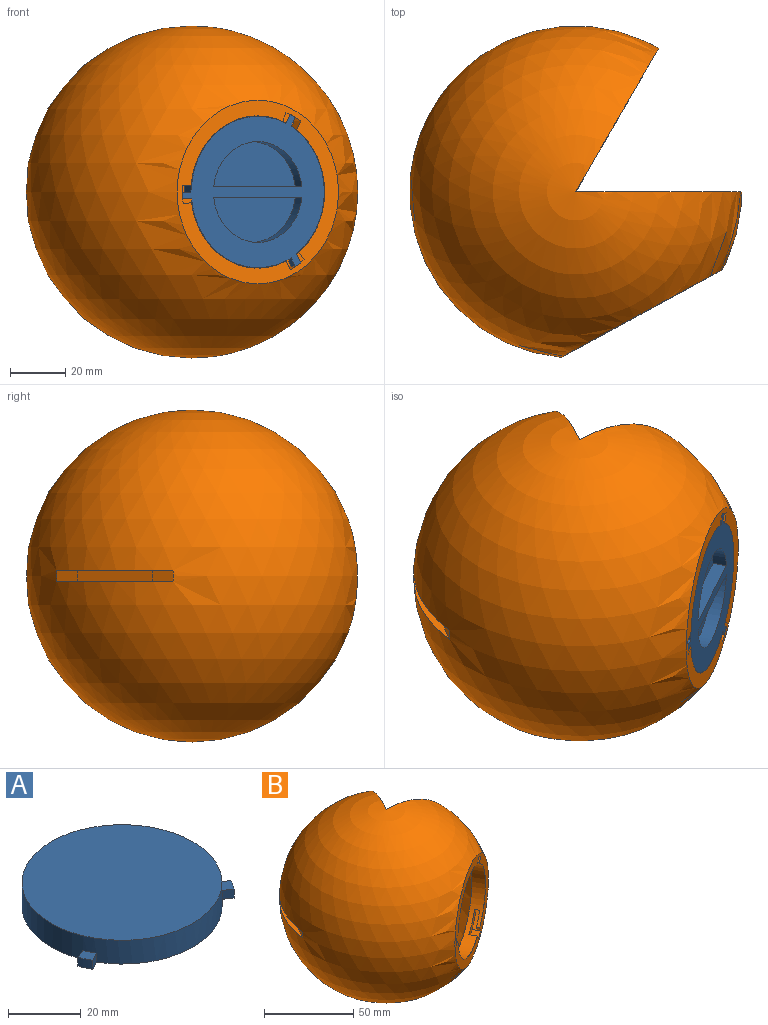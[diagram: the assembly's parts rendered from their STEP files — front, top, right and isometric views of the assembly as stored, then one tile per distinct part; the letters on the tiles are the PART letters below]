
ASSEMBLY  parts=2 mates=1
PART A: 21 faces, bbox 56.2x58.5x8 mm
  f0: plane 58.5x56.24mm, normal (0,0,-1), area 1519.9mm2, adj f1,f3,f4,f5,f7,f8,f9,f11
  f1: cylinder r=27.5mm len=55mm, axis (0,0,-1), area 1347.7mm2, adj f0,f2,f3,f4,f6,f7,f8,f10
  f2: plane 55x55mm, normal (0,0,1), area 2375.8mm2, adj f1
  f3: plane 3.5x3mm, normal (-1,0,0), area 10.5mm2, adj f0,f1,f5,f6
  f4: plane 3.47x3mm, normal (0.99,-0.14,0), area 10.5mm2, adj f0,f1,f5,f6
  f5: cylinder r=31mm len=4.31mm, axis (0,0,-1), area 13mm2, adj f0,f3,f4,f6
  f6: plane 4.31x3.77mm, normal (0,0,1), area 14.3mm2, adj f1,f3,f4,f5
  f7: plane 3.25x3mm, normal (-0.37,0.93,0), area 10.5mm2, adj f0,f1,f9,f10
  f8: plane 3.03x3mm, normal (0.5,-0.87,0), area 10.5mm2, adj f0,f1,f9,f10
  f9: cylinder r=31mm len=3.89mm, axis (0,0,-1), area 13mm2, adj f0,f7,f8,f10
  f10: plane 5.2x4.93mm, normal (0,0,1), area 14.3mm2, adj f1,f7,f8,f9
  f11: plane 3x2.76mm, normal (-0.62,-0.79,0), area 10.5mm2, adj f0,f1,f13,f14
  f12: plane 3.03x3mm, normal (0.5,0.87,0), area 10.5mm2, adj f0,f1,f13,f14
  f13: cylinder r=31mm len=3.59mm, axis (0,0,-1), area 13mm2, adj f0,f11,f12,f14
  f14: plane 5.34x5.18mm, normal (0,0,1), area 14.3mm2, adj f1,f11,f12,f13
  f15: plane 36.25x5mm, normal (1,0,0), area 181.2mm2, adj f0,f16,f17
  f16: cylinder r=18.23mm len=36.25mm, axis (0,0,-1), area 266.4mm2, adj f0,f15,f17
  f17: plane 36.25x16.23mm, normal (0,0,-1), area 449.4mm2, adj f15,f16
  f18: plane 36.25x5mm, normal (-1,0,0), area 181.2mm2, adj f0,f19,f20
  f19: cylinder r=18.23mm len=36.25mm, axis (0,0,-1), area 266.4mm2, adj f0,f18,f20
  f20: plane 36.25x16.23mm, normal (0,0,-1), area 449.4mm2, adj f18,f19
PART B: 38 faces, bbox 120x120x120 mm
  f0: plane 5.75x4.44mm, normal (0,0,1), area 7.7mm2, adj f5,f6,f7,f26,f27,f36,f37
  f1: plane 5.31x3.31mm, normal (0.76,0.41,-0.5), area 7.7mm2, adj f3,f6,f7,f23,f25,f33,f34
  f2: plane 5.31x3.31mm, normal (-0.76,-0.41,-0.5), area 7.7mm2, adj f4,f6,f7,f20,f22,f30,f31
  f3: sphere r=57mm, area 7.9mm2, adj f1,f6,f7,f28
  f4: sphere r=57mm, area 7.9mm2, adj f2,f6,f7,f24
  f5: sphere r=57mm, area 7.9mm2, adj f0,f6,f7,f21
  f6: plane 66.33x58.27mm, normal (0.48,-0.88,0), area 1046.5mm2, adj f0,f1,f2,f3,f4,f5,f8,f21
  f7: cylinder r=27.5mm len=55mm, axis (0.48,-0.88,0), area 1204.7mm2, adj f0,f1,f2,f3,f4,f5,f19,f20
  f8: sphere r=60mm, area 33727mm2, adj f6,f10,f11,f14,f15,f16,f17
  f9: sphere r=57mm, area 29129.7mm2, adj f12,f13,f14,f15,f16,f17,f18
  f10: plane 120x51.96mm, normal (0.87,-0.5,0), area 5654.9mm2, adj f8,f11
  f11: plane 120x60mm, normal (0,1,0), area 5654.9mm2, adj f8,f10
  f12: plane 113.84x53.8mm, normal (-0.87,0.5,0), area 5680.1mm2, adj f9,f13
  f13: plane 113.84x62.12mm, normal (0,-1,0), area 5680.1mm2, adj f9,f12
  f14: plane 7.61x4.5mm, normal (-0.86,0.51,0), area 34.9mm2, adj f8,f9,f16,f17
  f15: plane 7.61x4.5mm, normal (-0.86,0.51,0), area 34.9mm2, adj f8,f9,f16,f17
  f16: plane 42.02x24.85mm, normal (0,0,1), area 124.6mm2, adj f8,f9,f14,f15
  f17: plane 42.02x24.85mm, normal (0,0,-1), area 124.6mm2, adj f8,f9,f14,f15
  f18: cylinder r=32.5mm len=65mm, axis (0.48,-0.88,0), area 985.7mm2, adj f9,f19
  f19: plane 65x57.09mm, normal (-0.48,0.88,0), area 942.5mm2, adj f7,f18
  f20: plane 12.91x12.58mm, normal (0.48,-0.88,0), area 57.2mm2, adj f2,f7,f21,f22,f29,f30
  f21: plane 5.31x4.01mm, normal (0.76,0.41,0.5), area 18.5mm2, adj f5,f6,f7,f20,f22
  f22: plane 6.46x6.19mm, normal (-0.44,-0.24,0.87), area 25mm2, adj f2,f6,f20,f21
  f23: plane 13.99x8.55mm, normal (0.48,-0.88,0), area 57.2mm2, adj f1,f7,f24,f25,f32,f33
  f24: plane 5.31x4.01mm, normal (-0.76,-0.41,0.5), area 18.5mm2, adj f4,f6,f7,f23,f25
  f25: plane 6.46x6.19mm, normal (-0.44,-0.24,-0.87), area 25mm2, adj f1,f6,f23,f24
  f26: plane 16.27x5.64mm, normal (0.48,-0.88,0), area 57.2mm2, adj f0,f7,f27,f28,f35,f36
  f27: plane 5x4.39mm, normal (0.88,0.48,0), area 25mm2, adj f0,f6,f26,f28
  f28: plane 6.16x5.75mm, normal (0,0,-1), area 18.5mm2, adj f3,f6,f7,f26,f27
  f29: plane 4.06x4.05mm, normal (-0.49,-0.27,-0.83), area 10.7mm2, adj f7,f20,f30,f31
  f30: cylinder r=31.08mm len=8.64mm, axis (-0.48,0.88,0), area 35.3mm2, adj f2,f20,f29,f31
  f31: plane 10.32x8.78mm, normal (-0.48,0.88,0), area 39.1mm2, adj f2,f7,f29,f30
  f32: plane 3.57x2.75mm, normal (0.88,0.48,-0.06), area 10.7mm2, adj f7,f23,f33,f34
  f33: cylinder r=31.08mm len=11.38mm, axis (-0.48,0.88,0), area 35.3mm2, adj f1,f23,f32,f34
  f34: plane 10.14x6.05mm, normal (-0.48,0.88,0), area 39.1mm2, adj f1,f7,f32,f33
  f35: plane 4.25x4.17mm, normal (-0.39,-0.21,0.9), area 10.7mm2, adj f7,f26,f36,f37
  f36: cylinder r=31.08mm len=11.27mm, axis (-0.48,0.88,0), area 35.3mm2, adj f0,f26,f35,f37
  f37: plane 11.27x5.55mm, normal (-0.48,0.88,0), area 39.1mm2, adj f0,f7,f35,f36
PLACE A rot(axis=(-0.65,0.39,0.65),137.6deg) t=(20.89,-35.1,15.95)mm
PLACE B t=(-2.99,8.79,15.95)mm
MATE cylindrical A.f1 <-> B.f7  axis (0.48,-0.88,0) through (18.98,-31.58,15.95)mm
